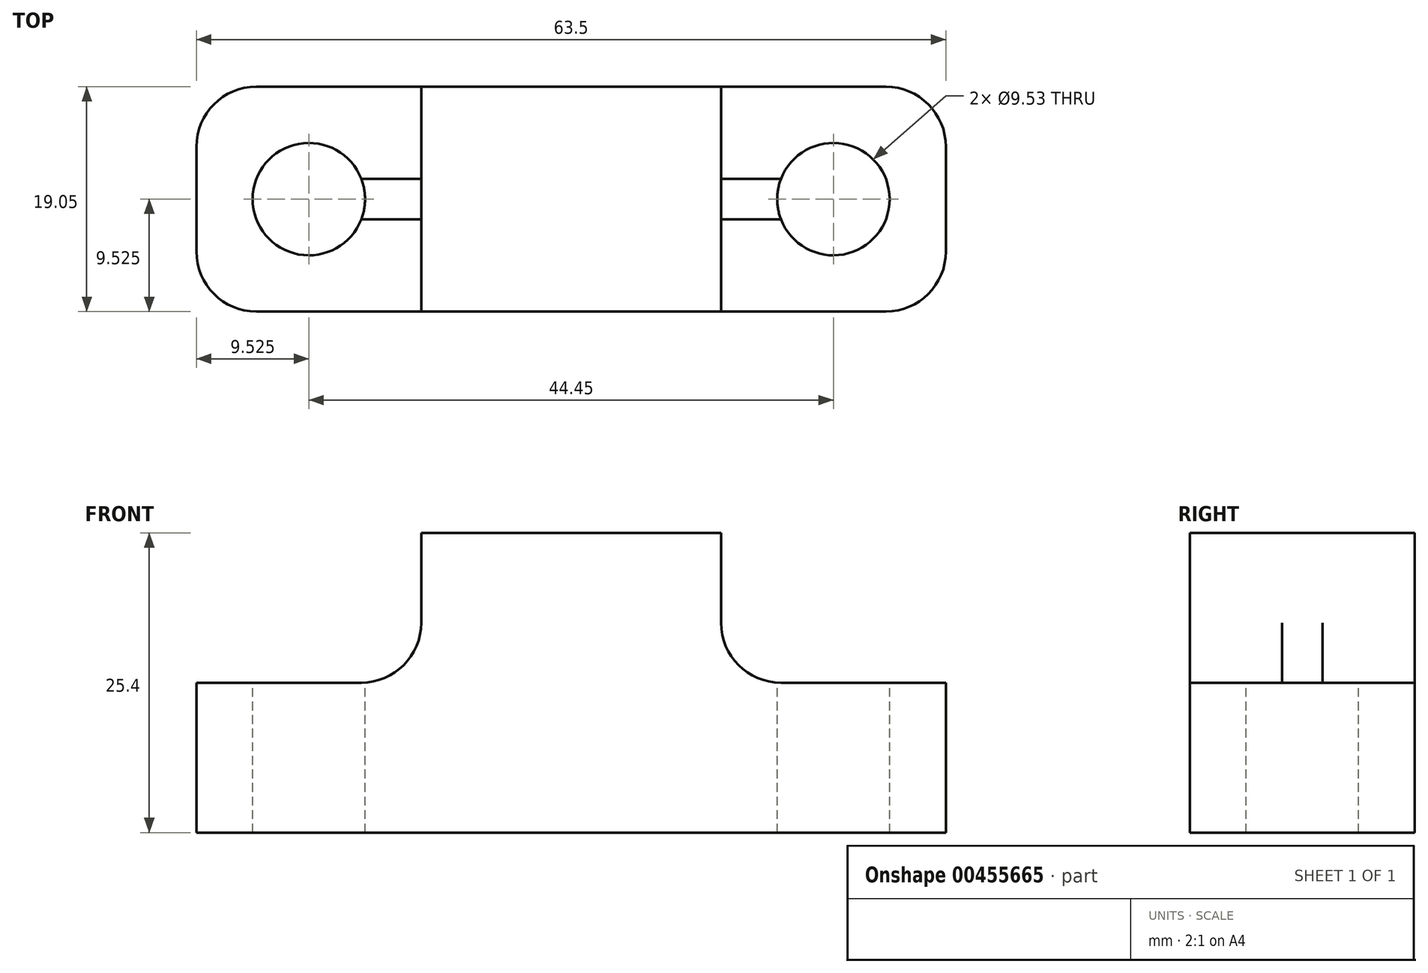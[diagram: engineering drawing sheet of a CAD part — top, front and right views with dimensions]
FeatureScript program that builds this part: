
annotation { "Feature Type Name" : "Feature", "Feature Type Description" : "" }
export const myFeature = defineFeature(function(context is Context, id is Id, definition is map)
    precondition{}
    {
        {
            var Q0;
            Q0=qCreatedBy(makeId("Front.planeOp"),FACE);
            var sketch = newSketch(context, id + "F0", { "sketchPlane" : qUnion([Q0])});
            skLineSegment(sketch, "E0.bottom", {"start": v(0, 0) * mm, "end": v(31.75, 0) * mm});
            skLineSegment(sketch, "E0.top", {"start": v(0, 25.4) * mm, "end": v(31.75, 25.4) * mm});
            skLineSegment(sketch, "E0.left", {"start": v(0, 0) * mm, "end": v(0, 25.4) * mm});
            skLineSegment(sketch, "E0.right", {"start": v(31.75, 0) * mm, "end": v(31.75, 25.4) * mm});
            skLineSegment(sketch, "E1.bottom", {"start": v(0, 25.4) * mm, "end": v(19.05, 25.4) * mm});
            skLineSegment(sketch, "E1.top", {"start": v(0, 12.7) * mm, "end": v(19.05, 12.7) * mm});
            skLineSegment(sketch, "E1.left", {"start": v(0, 25.4) * mm, "end": v(0, 12.7) * mm});
            skLineSegment(sketch, "E1.right", {"start": v(19.05, 25.4) * mm, "end": v(19.05, 12.7) * mm});
            skSolve(sketch);
        }
        {
            var Q0;
            Q0=makeQuery(id+"F0.imprint","IMPRINT",FACE,{"disambiguationData":[TD([[makeQuery(id+"F0.imprint","IMPRINT",EDGE,{"derivedFrom":sQuery(id+"F0.wireOp",EDGE,"E0.bottom")}),1.0]])]});
            extrude(context, id + "F1", {"entities" : qUnion([Q0]), "depth" : 19.05 * mm});
        }
        {
            var Q0;
            Q0=makeQuery(id+"F1.opExtrude","SWEPT_FACE",FACE,{"disambiguationData":[OSD([sQuery(id+"F0.wireOp",EDGE,"E1.top")])]});
            var sketch = newSketch(context, id + "F2", { "sketchPlane" : qUnion([Q0])});
            skLineSegment(sketch, "E2.bottom", {"start": v(0, 0) * mm, "end": v(9.53, 0) * mm});
            skLineSegment(sketch, "E2.top", {"start": v(0, -9.53) * mm, "end": v(9.53, -9.53) * mm});
            skLineSegment(sketch, "E2.left", {"start": v(0, 0) * mm, "end": v(0, -9.53) * mm});
            skLineSegment(sketch, "E2.right", {"start": v(9.53, 0) * mm, "end": v(9.53, -9.53) * mm});
            skCircle(sketch, "E3", {"center": v(9.53, -9.53) * mm, "radius": 4.76 * mm});
            skSolve(sketch);
        }
        {
            var Q0;
            {var subQ0=sQuery(id+"F2.wireOp",EDGE,"E2.right");var subQ1=sQuery(id+"F2.wireOp",EDGE,"E2.top");var subQ2=makeQuery(id+"F2.imprint","INTERSECT",VERTEX,{"derivedFrom":[subQ1,subQ0]});Q0=makeQuery(id+"F2.imprint","IMPRINT",FACE,{"disambiguationData":[TD([[makeQuery(id+"F2.imprint","IMPRINT",EDGE,{"disambiguationData":[TD([[subQ2,1.0]])],"derivedFrom":subQ1}),-1.0]])]});}
            var Q1;
            {var subQ0=sQuery(id+"F2.wireOp",EDGE,"E2.right");var subQ1=sQuery(id+"F2.wireOp",EDGE,"E2.top");var subQ2=makeQuery(id+"F2.imprint","INTERSECT",VERTEX,{"derivedFrom":[subQ1,subQ0]});Q1=makeQuery(id+"F2.imprint","IMPRINT",FACE,{"disambiguationData":[TD([[makeQuery(id+"F2.imprint","IMPRINT",EDGE,{"disambiguationData":[TD([[subQ2,1.0]])],"derivedFrom":subQ1}),1.0]])]});}
            extrude(context, id + "F3", {"entities" : qUnion([Q0, Q1]), "operationType" : NewBodyOperationType.REMOVE, "oppositeDirection" : true, "depth" : 25.4 * mm});
        }
        {
            var Q0;
            Q0=makeQuery(id+"F1.opExtrude","CAP_EDGE",EDGE,{"disambiguationData":[OSD([sQuery(id+"F0.wireOp",EDGE,"E0.left")])],"isStart":false});
            var Q1;
            Q1=makeQuery(id+"F1.opExtrude","CAP_EDGE",EDGE,{"disambiguationData":[OSD([sQuery(id+"F0.wireOp",EDGE,"E0.left")])],"isStart":true});
            var Q2;
            Q2=makeQuery(id+"F1.opExtrude","SWEPT_EDGE",EDGE,{"disambiguationData":[OSD([sQuery(id+"F0.wireOp",EDGE,"E1.top"),sQuery(id+"F0.wireOp",EDGE,"E1.right")])]});
            fillet(context, id + "F4", {"entities" : qUnion([Q0, Q1, Q2]), "radius" : 5.08 * mm, "tangentPropagation" : true, "allowEdgeOverflow" : false});
        }
        {
            var Q0;
            Q0=makeQuery(id+"F1.opExtrude","SWEPT_BODY",BODY,{"disambiguationData":[OSD([sQuery(id+"F0.wireOp",EDGE,"E0.bottom"),sQuery(id+"F0.wireOp",EDGE,"E0.top"),sQuery(id+"F0.wireOp",EDGE,"E0.left"),sQuery(id+"F0.wireOp",EDGE,"E0.right"),sQuery(id+"F0.wireOp",EDGE,"E1.top"),sQuery(id+"F0.wireOp",EDGE,"E1.right")])]});
            var Q1;
            Q1=makeQuery(id+"F1.opExtrude","SWEPT_FACE",FACE,{"disambiguationData":[OSD([sQuery(id+"F0.wireOp",EDGE,"E0.right")])]});
            mirror(context, id + "F5", {"operationType" : NewBodyOperationType.ADD, "entities" : qUnion([Q0]), "mirrorPlane" : qUnion([Q1])});
        }
    });
